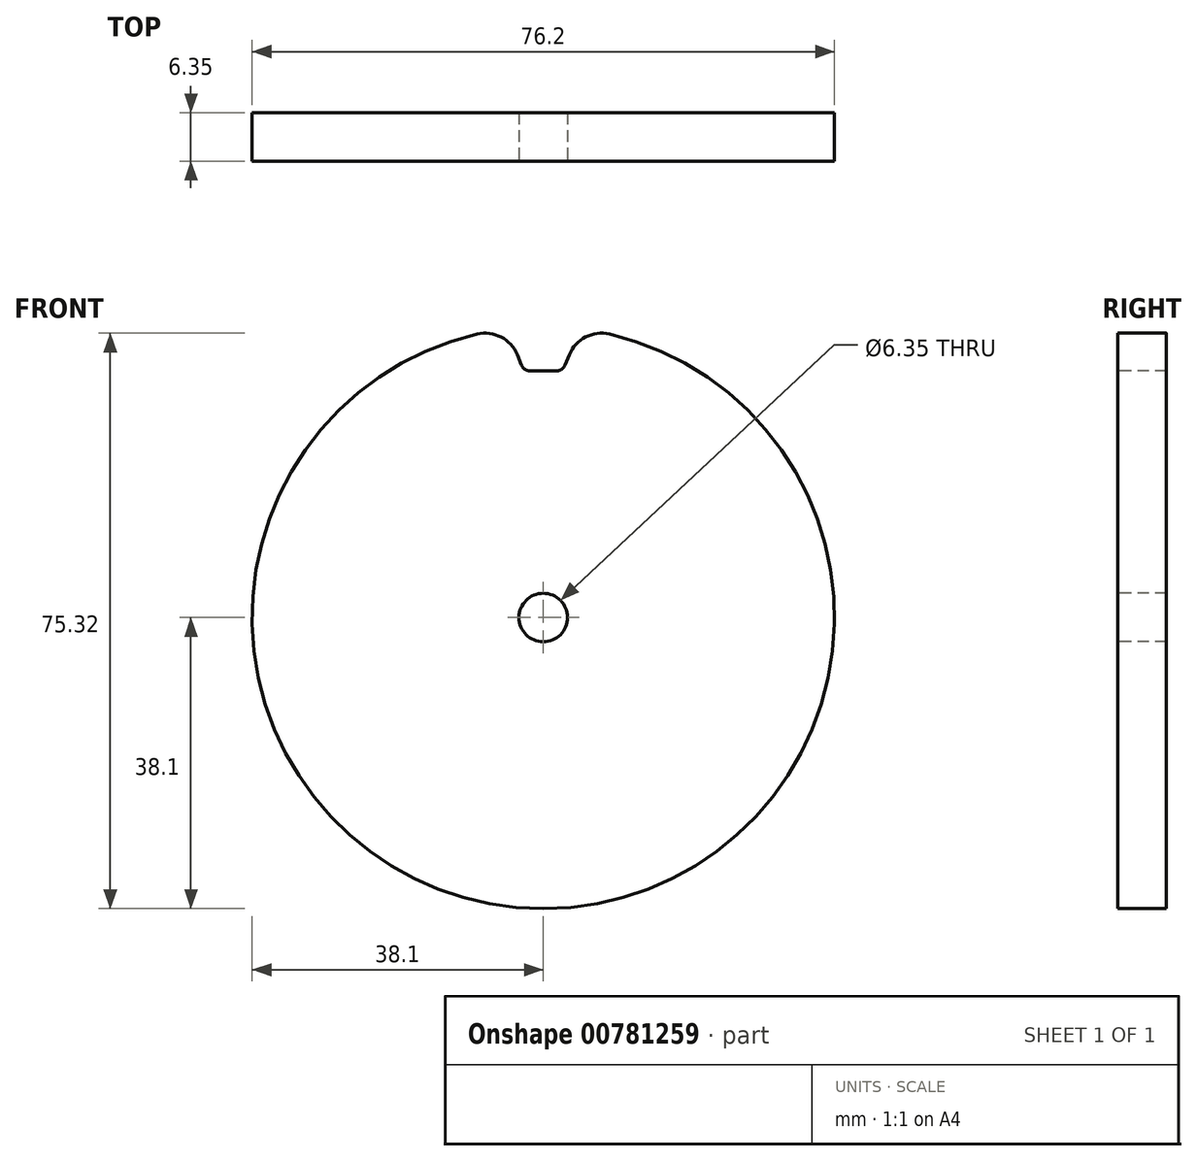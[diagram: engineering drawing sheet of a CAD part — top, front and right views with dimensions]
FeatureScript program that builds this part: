
annotation { "Feature Type Name" : "Feature", "Feature Type Description" : "" }
export const myFeature = defineFeature(function(context is Context, id is Id, definition is map)
    precondition{}
    {
        {
            var Q0;
            Q0=qCreatedBy(makeId("Right.planeOp"),FACE);
            var sketch = newSketch(context, id + "F0", { "sketchPlane" : qUnion([Q0])});
            skLineSegment(sketch, "E0", {"start": v(0, 0) * mm, "end": v(0, 76.2) * mm});
            skLineSegment(sketch, "E1", {"start": v(0, 76.2) * mm, "end": v(6.35, 76.2) * mm});
            skLineSegment(sketch, "E2", {"start": v(6.35, 76.2) * mm, "end": v(6.35, 0) * mm});
            skLineSegment(sketch, "E3", {"start": v(6.35, 0) * mm, "end": v(0, 0) * mm});
            skLineSegment(sketch, "E4", {"start": v(0, 38.1) * mm, "end": v(6.35, 38.1) * mm});
            skSolve(sketch);
        }
        {
            var Q0;
            {var subQ0=sQuery(id+"F0.wireOp",EDGE,"E1");Q0=makeQuery(id+"F0.imprint","IMPRINT",FACE,{"disambiguationData":[TD([[makeQuery(id+"F0.imprint","IMPRINT",EDGE,{"derivedFrom":subQ0}),-1.0]])]});}
            var Q1;
            Q1=sQuery(id+"F0.wireOp",EDGE,"E4");
            revolve(context, id + "F1", {"surfaceOperationType" : NewSurfaceOperationType.NEW, "entities" : qUnion([Q0]), "axis" : qUnion([Q1]), "revolveType" : RevolveType.FULL});
        }
        {
            var Q0;
            Q0=qCreatedBy(makeId("Front.planeOp"),FACE);
            var sketch = newSketch(context, id + "F2", { "sketchPlane" : qUnion([Q0])});
            skLineSegment(sketch, "E5", {"start": v(0, 0) * mm, "end": v(0, 76.2) * mm});
            skLineSegment(sketch, "E6", {"start": v(0, 70.36) * mm, "end": v(1.69, 70.36) * mm});
            skLineSegment(sketch, "E7", {"start": v(2.86, 71.16) * mm, "end": v(4.92, 76.2) * mm});
            skLineSegment(sketch, "E8.MirrorCS", {"start": v(0, 70.36) * mm, "end": v(-1.69, 70.36) * mm});
            skLineSegment(sketch, "E9.MirrorCS", {"start": v(-2.86, 71.16) * mm, "end": v(-4.92, 76.2) * mm});
            skLineSegment(sketch, "E10", {"start": v(-4.92, 76.2) * mm, "end": v(0, 76.2) * mm});
            skLineSegment(sketch, "E11", {"start": v(4.92, 76.2) * mm, "end": v(0, 76.2) * mm});
            skPoint(sketch, "E12.visualSharp", {"position": v(2.54, 70.36) * mm});
            skArc(sketch, "E12.filletArc", {"start": v(1.69, 70.36) * mm, "mid": v(2.4, 70.58) * mm, "end": v(2.86, 71.16) * mm});
            skPoint(sketch, "E13.visualSharp", {"position": v(-2.54, 70.36) * mm});
            skArc(sketch, "E13.filletArc", {"start": v(-2.86, 71.16) * mm, "mid": v(-2.4, 70.58) * mm, "end": v(-1.69, 70.36) * mm});
            skSolve(sketch);
        }
        {
            var Q0;
            {var subQ2=sQuery(id+"F2.wireOp",EDGE,"E8.MirrorCS");Q0=makeQuery(id+"F2.imprint","IMPRINT",FACE,{"disambiguationData":[TD([[makeQuery(id+"F2.imprint","IMPRINT",EDGE,{"derivedFrom":subQ2}),-1.0]])]});}
            var Q1;
            {var subQ2=sQuery(id+"F2.wireOp",EDGE,"E6");Q1=makeQuery(id+"F2.imprint","IMPRINT",FACE,{"disambiguationData":[TD([[makeQuery(id+"F2.imprint","IMPRINT",EDGE,{"derivedFrom":subQ2}),1.0]])]});}
            extrude(context, id + "F3", {"entities" : qUnion([Q0, Q1]), "operationType" : NewBodyOperationType.REMOVE, "oppositeDirection" : true, "depth" : 6.35 * mm, "offsetDistance" : 25.4 * mm});
        }
        {
            var Q0;
            {var subQ0=sQuery(id+"F2.wireOp",EDGE,"E9.MirrorCS");var subQ4=makeQuery(id+"F3.boolean.opBoolean","COPY",FACE,{"derivedFrom":makeQuery(id+"F3.opExtrude","SWEPT_FACE",FACE,{"disambiguationData":[OSD([subQ0])]})});Q0=makeQuery(id+"FfLhC88wAqj1xS8_1.13.F3.boolean.opBoolean","INTERSECT",EDGE,{"derivedFrom":[makeQuery(id+"FfLhC88wAqj1xS8_1.12.F3.boolean.opBoolean","SPLIT",FACE,{"disambiguationData":[TD([subQ4])],"derivedFrom":makeQuery(id+"FfLhC88wAqj1xS8_1.11.F3.boolean.opBoolean","SPLIT",FACE,{"disambiguationData":[TD([subQ4])],"derivedFrom":makeQuery(id+"FfLhC88wAqj1xS8_1.10.F3.boolean.opBoolean","SPLIT",FACE,{"disambiguationData":[TD([subQ4])],"derivedFrom":makeQuery(id+"FfLhC88wAqj1xS8_1.9.F3.boolean.opBoolean","SPLIT",FACE,{"disambiguationData":[TD([subQ4])],"derivedFrom":makeQuery(id+"FfLhC88wAqj1xS8_1.8.F3.boolean.opBoolean","SPLIT",FACE,{"disambiguationData":[TD([subQ4])],"derivedFrom":makeQuery(id+"FfLhC88wAqj1xS8_1.7.F3.boolean.opBoolean","SPLIT",FACE,{"disambiguationData":[TD([subQ4])],"derivedFrom":makeQuery(id+"FfLhC88wAqj1xS8_1.6.F3.boolean.opBoolean","SPLIT",FACE,{"disambiguationData":[TD([subQ4])],"derivedFrom":makeQuery(id+"FfLhC88wAqj1xS8_1.5.F3.boolean.opBoolean","SPLIT",FACE,{"disambiguationData":[TD([subQ4])],"derivedFrom":makeQuery(id+"FfLhC88wAqj1xS8_1.4.F3.boolean.opBoolean","SPLIT",FACE,{"disambiguationData":[TD([subQ4])],"derivedFrom":makeQuery(id+"FfLhC88wAqj1xS8_1.3.F3.boolean.opBoolean","SPLIT",FACE,{"disambiguationData":[TD([subQ4])],"derivedFrom":makeQuery(id+"FfLhC88wAqj1xS8_1.2.F3.boolean.opBoolean","SPLIT",FACE,{"disambiguationData":[TD([subQ4])],"derivedFrom":makeQuery(id+"FfLhC88wAqj1xS8_1.1.F3.boolean.opBoolean","SPLIT",FACE,{"disambiguationData":[TD([subQ4])],"derivedFrom":makeQuery(id+"F1.opRevolve","SWEPT_FACE",FACE,{"disambiguationData":[OSD([sQuery(id+"F0.wireOp",EDGE,"E1")])]})})})})})})})})})})})})}),makeQuery(id+"FfLhC88wAqj1xS8_1.13.F3.opExtrude","SWEPT_FACE",FACE,{"disambiguationData":[OSD([subQ0])]})]});}
            var Q1;
            {var subQ0=sQuery(id+"F2.wireOp",EDGE,"E7");var subQ3=makeQuery(id+"F3.boolean.opBoolean","COPY",FACE,{"derivedFrom":makeQuery(id+"F3.opExtrude","SWEPT_FACE",FACE,{"disambiguationData":[OSD([sQuery(id+"F2.wireOp",EDGE,"E9.MirrorCS")])]})});Q1=makeQuery(id+"FfLhC88wAqj1xS8_1.13.F3.boolean.opBoolean","INTERSECT",EDGE,{"derivedFrom":[makeQuery(id+"FfLhC88wAqj1xS8_1.12.F3.boolean.opBoolean","SPLIT",FACE,{"disambiguationData":[TD([subQ3])],"derivedFrom":makeQuery(id+"FfLhC88wAqj1xS8_1.11.F3.boolean.opBoolean","SPLIT",FACE,{"disambiguationData":[TD([subQ3])],"derivedFrom":makeQuery(id+"FfLhC88wAqj1xS8_1.10.F3.boolean.opBoolean","SPLIT",FACE,{"disambiguationData":[TD([subQ3])],"derivedFrom":makeQuery(id+"FfLhC88wAqj1xS8_1.9.F3.boolean.opBoolean","SPLIT",FACE,{"disambiguationData":[TD([subQ3])],"derivedFrom":makeQuery(id+"FfLhC88wAqj1xS8_1.8.F3.boolean.opBoolean","SPLIT",FACE,{"disambiguationData":[TD([subQ3])],"derivedFrom":makeQuery(id+"FfLhC88wAqj1xS8_1.7.F3.boolean.opBoolean","SPLIT",FACE,{"disambiguationData":[TD([subQ3])],"derivedFrom":makeQuery(id+"FfLhC88wAqj1xS8_1.6.F3.boolean.opBoolean","SPLIT",FACE,{"disambiguationData":[TD([subQ3])],"derivedFrom":makeQuery(id+"FfLhC88wAqj1xS8_1.5.F3.boolean.opBoolean","SPLIT",FACE,{"disambiguationData":[TD([subQ3])],"derivedFrom":makeQuery(id+"FfLhC88wAqj1xS8_1.4.F3.boolean.opBoolean","SPLIT",FACE,{"disambiguationData":[TD([subQ3])],"derivedFrom":makeQuery(id+"FfLhC88wAqj1xS8_1.3.F3.boolean.opBoolean","SPLIT",FACE,{"disambiguationData":[TD([subQ3])],"derivedFrom":makeQuery(id+"FfLhC88wAqj1xS8_1.2.F3.boolean.opBoolean","SPLIT",FACE,{"disambiguationData":[TD([subQ3])],"derivedFrom":makeQuery(id+"FfLhC88wAqj1xS8_1.1.F3.boolean.opBoolean","SPLIT",FACE,{"disambiguationData":[TD([subQ3])],"derivedFrom":makeQuery(id+"F1.opRevolve","SWEPT_FACE",FACE,{"disambiguationData":[OSD([sQuery(id+"F0.wireOp",EDGE,"E1")])]})})})})})})})})})})})})}),makeQuery(id+"FfLhC88wAqj1xS8_1.13.F3.opExtrude","SWEPT_FACE",FACE,{"disambiguationData":[OSD([subQ0])]})]});}
            var Q2;
            {var subQ0=sQuery(id+"F2.wireOp",EDGE,"E9.MirrorCS");var subQ4=makeQuery(id+"F3.boolean.opBoolean","COPY",FACE,{"derivedFrom":makeQuery(id+"F3.opExtrude","SWEPT_FACE",FACE,{"disambiguationData":[OSD([subQ0])]})});Q2=makeQuery(id+"FfLhC88wAqj1xS8_1.14.F3.boolean.opBoolean","INTERSECT",EDGE,{"derivedFrom":[makeQuery(id+"FfLhC88wAqj1xS8_1.13.F3.boolean.opBoolean","SPLIT",FACE,{"disambiguationData":[TD([subQ4])],"derivedFrom":makeQuery(id+"FfLhC88wAqj1xS8_1.12.F3.boolean.opBoolean","SPLIT",FACE,{"disambiguationData":[TD([subQ4])],"derivedFrom":makeQuery(id+"FfLhC88wAqj1xS8_1.11.F3.boolean.opBoolean","SPLIT",FACE,{"disambiguationData":[TD([subQ4])],"derivedFrom":makeQuery(id+"FfLhC88wAqj1xS8_1.10.F3.boolean.opBoolean","SPLIT",FACE,{"disambiguationData":[TD([subQ4])],"derivedFrom":makeQuery(id+"FfLhC88wAqj1xS8_1.9.F3.boolean.opBoolean","SPLIT",FACE,{"disambiguationData":[TD([subQ4])],"derivedFrom":makeQuery(id+"FfLhC88wAqj1xS8_1.8.F3.boolean.opBoolean","SPLIT",FACE,{"disambiguationData":[TD([subQ4])],"derivedFrom":makeQuery(id+"FfLhC88wAqj1xS8_1.7.F3.boolean.opBoolean","SPLIT",FACE,{"disambiguationData":[TD([subQ4])],"derivedFrom":makeQuery(id+"FfLhC88wAqj1xS8_1.6.F3.boolean.opBoolean","SPLIT",FACE,{"disambiguationData":[TD([subQ4])],"derivedFrom":makeQuery(id+"FfLhC88wAqj1xS8_1.5.F3.boolean.opBoolean","SPLIT",FACE,{"disambiguationData":[TD([subQ4])],"derivedFrom":makeQuery(id+"FfLhC88wAqj1xS8_1.4.F3.boolean.opBoolean","SPLIT",FACE,{"disambiguationData":[TD([subQ4])],"derivedFrom":makeQuery(id+"FfLhC88wAqj1xS8_1.3.F3.boolean.opBoolean","SPLIT",FACE,{"disambiguationData":[TD([subQ4])],"derivedFrom":makeQuery(id+"FfLhC88wAqj1xS8_1.2.F3.boolean.opBoolean","SPLIT",FACE,{"disambiguationData":[TD([subQ4])],"derivedFrom":makeQuery(id+"FfLhC88wAqj1xS8_1.1.F3.boolean.opBoolean","SPLIT",FACE,{"disambiguationData":[TD([subQ4])],"derivedFrom":makeQuery(id+"F1.opRevolve","SWEPT_FACE",FACE,{"disambiguationData":[OSD([sQuery(id+"F0.wireOp",EDGE,"E1")])]})})})})})})})})})})})})})}),makeQuery(id+"FfLhC88wAqj1xS8_1.14.F3.opExtrude","SWEPT_FACE",FACE,{"disambiguationData":[OSD([subQ0])]})]});}
            var Q3;
            {var subQ0=sQuery(id+"F2.wireOp",EDGE,"E7");var subQ3=makeQuery(id+"F3.boolean.opBoolean","COPY",FACE,{"derivedFrom":makeQuery(id+"F3.opExtrude","SWEPT_FACE",FACE,{"disambiguationData":[OSD([sQuery(id+"F2.wireOp",EDGE,"E9.MirrorCS")])]})});Q3=makeQuery(id+"FfLhC88wAqj1xS8_1.14.F3.boolean.opBoolean","INTERSECT",EDGE,{"derivedFrom":[makeQuery(id+"FfLhC88wAqj1xS8_1.13.F3.boolean.opBoolean","SPLIT",FACE,{"disambiguationData":[TD([subQ3])],"derivedFrom":makeQuery(id+"FfLhC88wAqj1xS8_1.12.F3.boolean.opBoolean","SPLIT",FACE,{"disambiguationData":[TD([subQ3])],"derivedFrom":makeQuery(id+"FfLhC88wAqj1xS8_1.11.F3.boolean.opBoolean","SPLIT",FACE,{"disambiguationData":[TD([subQ3])],"derivedFrom":makeQuery(id+"FfLhC88wAqj1xS8_1.10.F3.boolean.opBoolean","SPLIT",FACE,{"disambiguationData":[TD([subQ3])],"derivedFrom":makeQuery(id+"FfLhC88wAqj1xS8_1.9.F3.boolean.opBoolean","SPLIT",FACE,{"disambiguationData":[TD([subQ3])],"derivedFrom":makeQuery(id+"FfLhC88wAqj1xS8_1.8.F3.boolean.opBoolean","SPLIT",FACE,{"disambiguationData":[TD([subQ3])],"derivedFrom":makeQuery(id+"FfLhC88wAqj1xS8_1.7.F3.boolean.opBoolean","SPLIT",FACE,{"disambiguationData":[TD([subQ3])],"derivedFrom":makeQuery(id+"FfLhC88wAqj1xS8_1.6.F3.boolean.opBoolean","SPLIT",FACE,{"disambiguationData":[TD([subQ3])],"derivedFrom":makeQuery(id+"FfLhC88wAqj1xS8_1.5.F3.boolean.opBoolean","SPLIT",FACE,{"disambiguationData":[TD([subQ3])],"derivedFrom":makeQuery(id+"FfLhC88wAqj1xS8_1.4.F3.boolean.opBoolean","SPLIT",FACE,{"disambiguationData":[TD([subQ3])],"derivedFrom":makeQuery(id+"FfLhC88wAqj1xS8_1.3.F3.boolean.opBoolean","SPLIT",FACE,{"disambiguationData":[TD([subQ3])],"derivedFrom":makeQuery(id+"FfLhC88wAqj1xS8_1.2.F3.boolean.opBoolean","SPLIT",FACE,{"disambiguationData":[TD([subQ3])],"derivedFrom":makeQuery(id+"FfLhC88wAqj1xS8_1.1.F3.boolean.opBoolean","SPLIT",FACE,{"disambiguationData":[TD([subQ3])],"derivedFrom":makeQuery(id+"F1.opRevolve","SWEPT_FACE",FACE,{"disambiguationData":[OSD([sQuery(id+"F0.wireOp",EDGE,"E1")])]})})})})})})})})})})})})})}),makeQuery(id+"FfLhC88wAqj1xS8_1.14.F3.opExtrude","SWEPT_FACE",FACE,{"disambiguationData":[OSD([subQ0])]})]});}
            var Q4;
            {var subQ0=sQuery(id+"F2.wireOp",EDGE,"E9.MirrorCS");var subQ3=makeQuery(id+"F3.boolean.opBoolean","COPY",FACE,{"derivedFrom":makeQuery(id+"F3.opExtrude","SWEPT_FACE",FACE,{"disambiguationData":[OSD([subQ0])]})});Q4=makeQuery(id+"FfLhC88wAqj1xS8_1.15.F3.boolean.opBoolean","INTERSECT",EDGE,{"derivedFrom":[makeQuery(id+"FfLhC88wAqj1xS8_1.14.F3.boolean.opBoolean","SPLIT",FACE,{"disambiguationData":[TD([subQ3])],"derivedFrom":makeQuery(id+"FfLhC88wAqj1xS8_1.13.F3.boolean.opBoolean","SPLIT",FACE,{"disambiguationData":[TD([subQ3])],"derivedFrom":makeQuery(id+"FfLhC88wAqj1xS8_1.12.F3.boolean.opBoolean","SPLIT",FACE,{"disambiguationData":[TD([subQ3])],"derivedFrom":makeQuery(id+"FfLhC88wAqj1xS8_1.11.F3.boolean.opBoolean","SPLIT",FACE,{"disambiguationData":[TD([subQ3])],"derivedFrom":makeQuery(id+"FfLhC88wAqj1xS8_1.10.F3.boolean.opBoolean","SPLIT",FACE,{"disambiguationData":[TD([subQ3])],"derivedFrom":makeQuery(id+"FfLhC88wAqj1xS8_1.9.F3.boolean.opBoolean","SPLIT",FACE,{"disambiguationData":[TD([subQ3])],"derivedFrom":makeQuery(id+"FfLhC88wAqj1xS8_1.8.F3.boolean.opBoolean","SPLIT",FACE,{"disambiguationData":[TD([subQ3])],"derivedFrom":makeQuery(id+"FfLhC88wAqj1xS8_1.7.F3.boolean.opBoolean","SPLIT",FACE,{"disambiguationData":[TD([subQ3])],"derivedFrom":makeQuery(id+"FfLhC88wAqj1xS8_1.6.F3.boolean.opBoolean","SPLIT",FACE,{"disambiguationData":[TD([subQ3])],"derivedFrom":makeQuery(id+"FfLhC88wAqj1xS8_1.5.F3.boolean.opBoolean","SPLIT",FACE,{"disambiguationData":[TD([subQ3])],"derivedFrom":makeQuery(id+"FfLhC88wAqj1xS8_1.4.F3.boolean.opBoolean","SPLIT",FACE,{"disambiguationData":[TD([subQ3])],"derivedFrom":makeQuery(id+"FfLhC88wAqj1xS8_1.3.F3.boolean.opBoolean","SPLIT",FACE,{"disambiguationData":[TD([subQ3])],"derivedFrom":makeQuery(id+"FfLhC88wAqj1xS8_1.2.F3.boolean.opBoolean","SPLIT",FACE,{"disambiguationData":[TD([subQ3])],"derivedFrom":makeQuery(id+"FfLhC88wAqj1xS8_1.1.F3.boolean.opBoolean","SPLIT",FACE,{"disambiguationData":[TD([subQ3])],"derivedFrom":makeQuery(id+"F1.opRevolve","SWEPT_FACE",FACE,{"disambiguationData":[OSD([sQuery(id+"F0.wireOp",EDGE,"E1")])]})})})})})})})})})})})})})})}),makeQuery(id+"FfLhC88wAqj1xS8_1.15.F3.opExtrude","SWEPT_FACE",FACE,{"disambiguationData":[OSD([subQ0])]})]});}
            var Q5;
            {var subQ0=sQuery(id+"F2.wireOp",EDGE,"E7");var subQ3=makeQuery(id+"F3.boolean.opBoolean","COPY",FACE,{"derivedFrom":makeQuery(id+"F3.opExtrude","SWEPT_FACE",FACE,{"disambiguationData":[OSD([sQuery(id+"F2.wireOp",EDGE,"E9.MirrorCS")])]})});Q5=makeQuery(id+"FfLhC88wAqj1xS8_1.15.F3.boolean.opBoolean","INTERSECT",EDGE,{"derivedFrom":[makeQuery(id+"FfLhC88wAqj1xS8_1.14.F3.boolean.opBoolean","SPLIT",FACE,{"disambiguationData":[TD([subQ3])],"derivedFrom":makeQuery(id+"FfLhC88wAqj1xS8_1.13.F3.boolean.opBoolean","SPLIT",FACE,{"disambiguationData":[TD([subQ3])],"derivedFrom":makeQuery(id+"FfLhC88wAqj1xS8_1.12.F3.boolean.opBoolean","SPLIT",FACE,{"disambiguationData":[TD([subQ3])],"derivedFrom":makeQuery(id+"FfLhC88wAqj1xS8_1.11.F3.boolean.opBoolean","SPLIT",FACE,{"disambiguationData":[TD([subQ3])],"derivedFrom":makeQuery(id+"FfLhC88wAqj1xS8_1.10.F3.boolean.opBoolean","SPLIT",FACE,{"disambiguationData":[TD([subQ3])],"derivedFrom":makeQuery(id+"FfLhC88wAqj1xS8_1.9.F3.boolean.opBoolean","SPLIT",FACE,{"disambiguationData":[TD([subQ3])],"derivedFrom":makeQuery(id+"FfLhC88wAqj1xS8_1.8.F3.boolean.opBoolean","SPLIT",FACE,{"disambiguationData":[TD([subQ3])],"derivedFrom":makeQuery(id+"FfLhC88wAqj1xS8_1.7.F3.boolean.opBoolean","SPLIT",FACE,{"disambiguationData":[TD([subQ3])],"derivedFrom":makeQuery(id+"FfLhC88wAqj1xS8_1.6.F3.boolean.opBoolean","SPLIT",FACE,{"disambiguationData":[TD([subQ3])],"derivedFrom":makeQuery(id+"FfLhC88wAqj1xS8_1.5.F3.boolean.opBoolean","SPLIT",FACE,{"disambiguationData":[TD([subQ3])],"derivedFrom":makeQuery(id+"FfLhC88wAqj1xS8_1.4.F3.boolean.opBoolean","SPLIT",FACE,{"disambiguationData":[TD([subQ3])],"derivedFrom":makeQuery(id+"FfLhC88wAqj1xS8_1.3.F3.boolean.opBoolean","SPLIT",FACE,{"disambiguationData":[TD([subQ3])],"derivedFrom":makeQuery(id+"FfLhC88wAqj1xS8_1.2.F3.boolean.opBoolean","SPLIT",FACE,{"disambiguationData":[TD([subQ3])],"derivedFrom":makeQuery(id+"FfLhC88wAqj1xS8_1.1.F3.boolean.opBoolean","SPLIT",FACE,{"disambiguationData":[TD([subQ3])],"derivedFrom":makeQuery(id+"F1.opRevolve","SWEPT_FACE",FACE,{"disambiguationData":[OSD([sQuery(id+"F0.wireOp",EDGE,"E1")])]})})})})})})})})})})})})})})}),makeQuery(id+"FfLhC88wAqj1xS8_1.15.F3.opExtrude","SWEPT_FACE",FACE,{"disambiguationData":[OSD([subQ0])]})]});}
            var Q6;
            Q6=makeQuery(id+"F3.boolean.opBoolean","INTERSECT",EDGE,{"derivedFrom":[makeQuery(id+"F1.opRevolve","SWEPT_FACE",FACE,{"disambiguationData":[OSD([sQuery(id+"F0.wireOp",EDGE,"E1")])]}),makeQuery(id+"F3.opExtrude","SWEPT_FACE",FACE,{"disambiguationData":[OSD([sQuery(id+"F2.wireOp",EDGE,"E9.MirrorCS")])]})]});
            var Q7;
            Q7=makeQuery(id+"F3.boolean.opBoolean","INTERSECT",EDGE,{"derivedFrom":[makeQuery(id+"F1.opRevolve","SWEPT_FACE",FACE,{"disambiguationData":[OSD([sQuery(id+"F0.wireOp",EDGE,"E1")])]}),makeQuery(id+"F3.opExtrude","SWEPT_FACE",FACE,{"disambiguationData":[OSD([sQuery(id+"F2.wireOp",EDGE,"E7")])]})]});
            var Q8;
            {var subQ0=sQuery(id+"F2.wireOp",EDGE,"E7");var subQ3=makeQuery(id+"F3.boolean.opBoolean","COPY",FACE,{"derivedFrom":makeQuery(id+"F3.opExtrude","SWEPT_FACE",FACE,{"disambiguationData":[OSD([sQuery(id+"F2.wireOp",EDGE,"E9.MirrorCS")])]})});Q8=makeQuery(id+"FfLhC88wAqj1xS8_1.12.F3.boolean.opBoolean","INTERSECT",EDGE,{"derivedFrom":[makeQuery(id+"FfLhC88wAqj1xS8_1.11.F3.boolean.opBoolean","SPLIT",FACE,{"disambiguationData":[TD([subQ3])],"derivedFrom":makeQuery(id+"FfLhC88wAqj1xS8_1.10.F3.boolean.opBoolean","SPLIT",FACE,{"disambiguationData":[TD([subQ3])],"derivedFrom":makeQuery(id+"FfLhC88wAqj1xS8_1.9.F3.boolean.opBoolean","SPLIT",FACE,{"disambiguationData":[TD([subQ3])],"derivedFrom":makeQuery(id+"FfLhC88wAqj1xS8_1.8.F3.boolean.opBoolean","SPLIT",FACE,{"disambiguationData":[TD([subQ3])],"derivedFrom":makeQuery(id+"FfLhC88wAqj1xS8_1.7.F3.boolean.opBoolean","SPLIT",FACE,{"disambiguationData":[TD([subQ3])],"derivedFrom":makeQuery(id+"FfLhC88wAqj1xS8_1.6.F3.boolean.opBoolean","SPLIT",FACE,{"disambiguationData":[TD([subQ3])],"derivedFrom":makeQuery(id+"FfLhC88wAqj1xS8_1.5.F3.boolean.opBoolean","SPLIT",FACE,{"disambiguationData":[TD([subQ3])],"derivedFrom":makeQuery(id+"FfLhC88wAqj1xS8_1.4.F3.boolean.opBoolean","SPLIT",FACE,{"disambiguationData":[TD([subQ3])],"derivedFrom":makeQuery(id+"FfLhC88wAqj1xS8_1.3.F3.boolean.opBoolean","SPLIT",FACE,{"disambiguationData":[TD([subQ3])],"derivedFrom":makeQuery(id+"FfLhC88wAqj1xS8_1.2.F3.boolean.opBoolean","SPLIT",FACE,{"disambiguationData":[TD([subQ3])],"derivedFrom":makeQuery(id+"FfLhC88wAqj1xS8_1.1.F3.boolean.opBoolean","SPLIT",FACE,{"disambiguationData":[TD([subQ3])],"derivedFrom":makeQuery(id+"F1.opRevolve","SWEPT_FACE",FACE,{"disambiguationData":[OSD([sQuery(id+"F0.wireOp",EDGE,"E1")])]})})})})})})})})})})})}),makeQuery(id+"FfLhC88wAqj1xS8_1.12.F3.opExtrude","SWEPT_FACE",FACE,{"disambiguationData":[OSD([subQ0])]})]});}
            var Q9;
            {var subQ0=sQuery(id+"F2.wireOp",EDGE,"E9.MirrorCS");var subQ3=makeQuery(id+"F3.boolean.opBoolean","COPY",FACE,{"derivedFrom":makeQuery(id+"F3.opExtrude","SWEPT_FACE",FACE,{"disambiguationData":[OSD([subQ0])]})});Q9=makeQuery(id+"FfLhC88wAqj1xS8_1.12.F3.boolean.opBoolean","INTERSECT",EDGE,{"derivedFrom":[makeQuery(id+"FfLhC88wAqj1xS8_1.11.F3.boolean.opBoolean","SPLIT",FACE,{"disambiguationData":[TD([subQ3])],"derivedFrom":makeQuery(id+"FfLhC88wAqj1xS8_1.10.F3.boolean.opBoolean","SPLIT",FACE,{"disambiguationData":[TD([subQ3])],"derivedFrom":makeQuery(id+"FfLhC88wAqj1xS8_1.9.F3.boolean.opBoolean","SPLIT",FACE,{"disambiguationData":[TD([subQ3])],"derivedFrom":makeQuery(id+"FfLhC88wAqj1xS8_1.8.F3.boolean.opBoolean","SPLIT",FACE,{"disambiguationData":[TD([subQ3])],"derivedFrom":makeQuery(id+"FfLhC88wAqj1xS8_1.7.F3.boolean.opBoolean","SPLIT",FACE,{"disambiguationData":[TD([subQ3])],"derivedFrom":makeQuery(id+"FfLhC88wAqj1xS8_1.6.F3.boolean.opBoolean","SPLIT",FACE,{"disambiguationData":[TD([subQ3])],"derivedFrom":makeQuery(id+"FfLhC88wAqj1xS8_1.5.F3.boolean.opBoolean","SPLIT",FACE,{"disambiguationData":[TD([subQ3])],"derivedFrom":makeQuery(id+"FfLhC88wAqj1xS8_1.4.F3.boolean.opBoolean","SPLIT",FACE,{"disambiguationData":[TD([subQ3])],"derivedFrom":makeQuery(id+"FfLhC88wAqj1xS8_1.3.F3.boolean.opBoolean","SPLIT",FACE,{"disambiguationData":[TD([subQ3])],"derivedFrom":makeQuery(id+"FfLhC88wAqj1xS8_1.2.F3.boolean.opBoolean","SPLIT",FACE,{"disambiguationData":[TD([subQ3])],"derivedFrom":makeQuery(id+"FfLhC88wAqj1xS8_1.1.F3.boolean.opBoolean","SPLIT",FACE,{"disambiguationData":[TD([subQ3])],"derivedFrom":makeQuery(id+"F1.opRevolve","SWEPT_FACE",FACE,{"disambiguationData":[OSD([sQuery(id+"F0.wireOp",EDGE,"E1")])]})})})})})})})})})})})}),makeQuery(id+"FfLhC88wAqj1xS8_1.12.F3.opExtrude","SWEPT_FACE",FACE,{"disambiguationData":[OSD([subQ0])]})]});}
            var Q10;
            {var subQ0=sQuery(id+"F2.wireOp",EDGE,"E7");var subQ3=makeQuery(id+"F3.boolean.opBoolean","COPY",FACE,{"derivedFrom":makeQuery(id+"F3.opExtrude","SWEPT_FACE",FACE,{"disambiguationData":[OSD([sQuery(id+"F2.wireOp",EDGE,"E9.MirrorCS")])]})});Q10=makeQuery(id+"FfLhC88wAqj1xS8_1.11.F3.boolean.opBoolean","INTERSECT",EDGE,{"derivedFrom":[makeQuery(id+"FfLhC88wAqj1xS8_1.10.F3.boolean.opBoolean","SPLIT",FACE,{"disambiguationData":[TD([subQ3])],"derivedFrom":makeQuery(id+"FfLhC88wAqj1xS8_1.9.F3.boolean.opBoolean","SPLIT",FACE,{"disambiguationData":[TD([subQ3])],"derivedFrom":makeQuery(id+"FfLhC88wAqj1xS8_1.8.F3.boolean.opBoolean","SPLIT",FACE,{"disambiguationData":[TD([subQ3])],"derivedFrom":makeQuery(id+"FfLhC88wAqj1xS8_1.7.F3.boolean.opBoolean","SPLIT",FACE,{"disambiguationData":[TD([subQ3])],"derivedFrom":makeQuery(id+"FfLhC88wAqj1xS8_1.6.F3.boolean.opBoolean","SPLIT",FACE,{"disambiguationData":[TD([subQ3])],"derivedFrom":makeQuery(id+"FfLhC88wAqj1xS8_1.5.F3.boolean.opBoolean","SPLIT",FACE,{"disambiguationData":[TD([subQ3])],"derivedFrom":makeQuery(id+"FfLhC88wAqj1xS8_1.4.F3.boolean.opBoolean","SPLIT",FACE,{"disambiguationData":[TD([subQ3])],"derivedFrom":makeQuery(id+"FfLhC88wAqj1xS8_1.3.F3.boolean.opBoolean","SPLIT",FACE,{"disambiguationData":[TD([subQ3])],"derivedFrom":makeQuery(id+"FfLhC88wAqj1xS8_1.2.F3.boolean.opBoolean","SPLIT",FACE,{"disambiguationData":[TD([subQ3])],"derivedFrom":makeQuery(id+"FfLhC88wAqj1xS8_1.1.F3.boolean.opBoolean","SPLIT",FACE,{"disambiguationData":[TD([subQ3])],"derivedFrom":makeQuery(id+"F1.opRevolve","SWEPT_FACE",FACE,{"disambiguationData":[OSD([sQuery(id+"F0.wireOp",EDGE,"E1")])]})})})})})})})})})})}),makeQuery(id+"FfLhC88wAqj1xS8_1.11.F3.opExtrude","SWEPT_FACE",FACE,{"disambiguationData":[OSD([subQ0])]})]});}
            var Q11;
            {var subQ0=sQuery(id+"F2.wireOp",EDGE,"E9.MirrorCS");var subQ3=makeQuery(id+"F3.boolean.opBoolean","COPY",FACE,{"derivedFrom":makeQuery(id+"F3.opExtrude","SWEPT_FACE",FACE,{"disambiguationData":[OSD([subQ0])]})});Q11=makeQuery(id+"FfLhC88wAqj1xS8_1.11.F3.boolean.opBoolean","INTERSECT",EDGE,{"derivedFrom":[makeQuery(id+"FfLhC88wAqj1xS8_1.10.F3.boolean.opBoolean","SPLIT",FACE,{"disambiguationData":[TD([subQ3])],"derivedFrom":makeQuery(id+"FfLhC88wAqj1xS8_1.9.F3.boolean.opBoolean","SPLIT",FACE,{"disambiguationData":[TD([subQ3])],"derivedFrom":makeQuery(id+"FfLhC88wAqj1xS8_1.8.F3.boolean.opBoolean","SPLIT",FACE,{"disambiguationData":[TD([subQ3])],"derivedFrom":makeQuery(id+"FfLhC88wAqj1xS8_1.7.F3.boolean.opBoolean","SPLIT",FACE,{"disambiguationData":[TD([subQ3])],"derivedFrom":makeQuery(id+"FfLhC88wAqj1xS8_1.6.F3.boolean.opBoolean","SPLIT",FACE,{"disambiguationData":[TD([subQ3])],"derivedFrom":makeQuery(id+"FfLhC88wAqj1xS8_1.5.F3.boolean.opBoolean","SPLIT",FACE,{"disambiguationData":[TD([subQ3])],"derivedFrom":makeQuery(id+"FfLhC88wAqj1xS8_1.4.F3.boolean.opBoolean","SPLIT",FACE,{"disambiguationData":[TD([subQ3])],"derivedFrom":makeQuery(id+"FfLhC88wAqj1xS8_1.3.F3.boolean.opBoolean","SPLIT",FACE,{"disambiguationData":[TD([subQ3])],"derivedFrom":makeQuery(id+"FfLhC88wAqj1xS8_1.2.F3.boolean.opBoolean","SPLIT",FACE,{"disambiguationData":[TD([subQ3])],"derivedFrom":makeQuery(id+"FfLhC88wAqj1xS8_1.1.F3.boolean.opBoolean","SPLIT",FACE,{"disambiguationData":[TD([subQ3])],"derivedFrom":makeQuery(id+"F1.opRevolve","SWEPT_FACE",FACE,{"disambiguationData":[OSD([sQuery(id+"F0.wireOp",EDGE,"E1")])]})})})})})})})})})})}),makeQuery(id+"FfLhC88wAqj1xS8_1.11.F3.opExtrude","SWEPT_FACE",FACE,{"disambiguationData":[OSD([subQ0])]})]});}
            var Q12;
            {var subQ0=sQuery(id+"F2.wireOp",EDGE,"E7");var subQ3=makeQuery(id+"F3.boolean.opBoolean","COPY",FACE,{"derivedFrom":makeQuery(id+"F3.opExtrude","SWEPT_FACE",FACE,{"disambiguationData":[OSD([sQuery(id+"F2.wireOp",EDGE,"E9.MirrorCS")])]})});Q12=makeQuery(id+"FfLhC88wAqj1xS8_1.10.F3.boolean.opBoolean","INTERSECT",EDGE,{"derivedFrom":[makeQuery(id+"FfLhC88wAqj1xS8_1.9.F3.boolean.opBoolean","SPLIT",FACE,{"disambiguationData":[TD([subQ3])],"derivedFrom":makeQuery(id+"FfLhC88wAqj1xS8_1.8.F3.boolean.opBoolean","SPLIT",FACE,{"disambiguationData":[TD([subQ3])],"derivedFrom":makeQuery(id+"FfLhC88wAqj1xS8_1.7.F3.boolean.opBoolean","SPLIT",FACE,{"disambiguationData":[TD([subQ3])],"derivedFrom":makeQuery(id+"FfLhC88wAqj1xS8_1.6.F3.boolean.opBoolean","SPLIT",FACE,{"disambiguationData":[TD([subQ3])],"derivedFrom":makeQuery(id+"FfLhC88wAqj1xS8_1.5.F3.boolean.opBoolean","SPLIT",FACE,{"disambiguationData":[TD([subQ3])],"derivedFrom":makeQuery(id+"FfLhC88wAqj1xS8_1.4.F3.boolean.opBoolean","SPLIT",FACE,{"disambiguationData":[TD([subQ3])],"derivedFrom":makeQuery(id+"FfLhC88wAqj1xS8_1.3.F3.boolean.opBoolean","SPLIT",FACE,{"disambiguationData":[TD([subQ3])],"derivedFrom":makeQuery(id+"FfLhC88wAqj1xS8_1.2.F3.boolean.opBoolean","SPLIT",FACE,{"disambiguationData":[TD([subQ3])],"derivedFrom":makeQuery(id+"FfLhC88wAqj1xS8_1.1.F3.boolean.opBoolean","SPLIT",FACE,{"disambiguationData":[TD([subQ3])],"derivedFrom":makeQuery(id+"F1.opRevolve","SWEPT_FACE",FACE,{"disambiguationData":[OSD([sQuery(id+"F0.wireOp",EDGE,"E1")])]})})})})})})})})})}),makeQuery(id+"FfLhC88wAqj1xS8_1.10.F3.opExtrude","SWEPT_FACE",FACE,{"disambiguationData":[OSD([subQ0])]})]});}
            var Q13;
            {var subQ0=sQuery(id+"F2.wireOp",EDGE,"E9.MirrorCS");var subQ3=makeQuery(id+"F3.boolean.opBoolean","COPY",FACE,{"derivedFrom":makeQuery(id+"F3.opExtrude","SWEPT_FACE",FACE,{"disambiguationData":[OSD([subQ0])]})});Q13=makeQuery(id+"FfLhC88wAqj1xS8_1.10.F3.boolean.opBoolean","INTERSECT",EDGE,{"derivedFrom":[makeQuery(id+"FfLhC88wAqj1xS8_1.9.F3.boolean.opBoolean","SPLIT",FACE,{"disambiguationData":[TD([subQ3])],"derivedFrom":makeQuery(id+"FfLhC88wAqj1xS8_1.8.F3.boolean.opBoolean","SPLIT",FACE,{"disambiguationData":[TD([subQ3])],"derivedFrom":makeQuery(id+"FfLhC88wAqj1xS8_1.7.F3.boolean.opBoolean","SPLIT",FACE,{"disambiguationData":[TD([subQ3])],"derivedFrom":makeQuery(id+"FfLhC88wAqj1xS8_1.6.F3.boolean.opBoolean","SPLIT",FACE,{"disambiguationData":[TD([subQ3])],"derivedFrom":makeQuery(id+"FfLhC88wAqj1xS8_1.5.F3.boolean.opBoolean","SPLIT",FACE,{"disambiguationData":[TD([subQ3])],"derivedFrom":makeQuery(id+"FfLhC88wAqj1xS8_1.4.F3.boolean.opBoolean","SPLIT",FACE,{"disambiguationData":[TD([subQ3])],"derivedFrom":makeQuery(id+"FfLhC88wAqj1xS8_1.3.F3.boolean.opBoolean","SPLIT",FACE,{"disambiguationData":[TD([subQ3])],"derivedFrom":makeQuery(id+"FfLhC88wAqj1xS8_1.2.F3.boolean.opBoolean","SPLIT",FACE,{"disambiguationData":[TD([subQ3])],"derivedFrom":makeQuery(id+"FfLhC88wAqj1xS8_1.1.F3.boolean.opBoolean","SPLIT",FACE,{"disambiguationData":[TD([subQ3])],"derivedFrom":makeQuery(id+"F1.opRevolve","SWEPT_FACE",FACE,{"disambiguationData":[OSD([sQuery(id+"F0.wireOp",EDGE,"E1")])]})})})})})})})})})}),makeQuery(id+"FfLhC88wAqj1xS8_1.10.F3.opExtrude","SWEPT_FACE",FACE,{"disambiguationData":[OSD([subQ0])]})]});}
            var Q14;
            {var subQ0=sQuery(id+"F2.wireOp",EDGE,"E7");var subQ3=makeQuery(id+"F3.boolean.opBoolean","COPY",FACE,{"derivedFrom":makeQuery(id+"F3.opExtrude","SWEPT_FACE",FACE,{"disambiguationData":[OSD([sQuery(id+"F2.wireOp",EDGE,"E9.MirrorCS")])]})});Q14=makeQuery(id+"FfLhC88wAqj1xS8_1.9.F3.boolean.opBoolean","INTERSECT",EDGE,{"derivedFrom":[makeQuery(id+"FfLhC88wAqj1xS8_1.8.F3.boolean.opBoolean","SPLIT",FACE,{"disambiguationData":[TD([subQ3])],"derivedFrom":makeQuery(id+"FfLhC88wAqj1xS8_1.7.F3.boolean.opBoolean","SPLIT",FACE,{"disambiguationData":[TD([subQ3])],"derivedFrom":makeQuery(id+"FfLhC88wAqj1xS8_1.6.F3.boolean.opBoolean","SPLIT",FACE,{"disambiguationData":[TD([subQ3])],"derivedFrom":makeQuery(id+"FfLhC88wAqj1xS8_1.5.F3.boolean.opBoolean","SPLIT",FACE,{"disambiguationData":[TD([subQ3])],"derivedFrom":makeQuery(id+"FfLhC88wAqj1xS8_1.4.F3.boolean.opBoolean","SPLIT",FACE,{"disambiguationData":[TD([subQ3])],"derivedFrom":makeQuery(id+"FfLhC88wAqj1xS8_1.3.F3.boolean.opBoolean","SPLIT",FACE,{"disambiguationData":[TD([subQ3])],"derivedFrom":makeQuery(id+"FfLhC88wAqj1xS8_1.2.F3.boolean.opBoolean","SPLIT",FACE,{"disambiguationData":[TD([subQ3])],"derivedFrom":makeQuery(id+"FfLhC88wAqj1xS8_1.1.F3.boolean.opBoolean","SPLIT",FACE,{"disambiguationData":[TD([subQ3])],"derivedFrom":makeQuery(id+"F1.opRevolve","SWEPT_FACE",FACE,{"disambiguationData":[OSD([sQuery(id+"F0.wireOp",EDGE,"E1")])]})})})})})})})})}),makeQuery(id+"FfLhC88wAqj1xS8_1.9.F3.opExtrude","SWEPT_FACE",FACE,{"disambiguationData":[OSD([subQ0])]})]});}
            var Q15;
            {var subQ0=sQuery(id+"F2.wireOp",EDGE,"E9.MirrorCS");var subQ4=makeQuery(id+"F3.boolean.opBoolean","COPY",FACE,{"derivedFrom":makeQuery(id+"F3.opExtrude","SWEPT_FACE",FACE,{"disambiguationData":[OSD([subQ0])]})});Q15=makeQuery(id+"FfLhC88wAqj1xS8_1.9.F3.boolean.opBoolean","INTERSECT",EDGE,{"derivedFrom":[makeQuery(id+"FfLhC88wAqj1xS8_1.8.F3.boolean.opBoolean","SPLIT",FACE,{"disambiguationData":[TD([subQ4])],"derivedFrom":makeQuery(id+"FfLhC88wAqj1xS8_1.7.F3.boolean.opBoolean","SPLIT",FACE,{"disambiguationData":[TD([subQ4])],"derivedFrom":makeQuery(id+"FfLhC88wAqj1xS8_1.6.F3.boolean.opBoolean","SPLIT",FACE,{"disambiguationData":[TD([subQ4])],"derivedFrom":makeQuery(id+"FfLhC88wAqj1xS8_1.5.F3.boolean.opBoolean","SPLIT",FACE,{"disambiguationData":[TD([subQ4])],"derivedFrom":makeQuery(id+"FfLhC88wAqj1xS8_1.4.F3.boolean.opBoolean","SPLIT",FACE,{"disambiguationData":[TD([subQ4])],"derivedFrom":makeQuery(id+"FfLhC88wAqj1xS8_1.3.F3.boolean.opBoolean","SPLIT",FACE,{"disambiguationData":[TD([subQ4])],"derivedFrom":makeQuery(id+"FfLhC88wAqj1xS8_1.2.F3.boolean.opBoolean","SPLIT",FACE,{"disambiguationData":[TD([subQ4])],"derivedFrom":makeQuery(id+"FfLhC88wAqj1xS8_1.1.F3.boolean.opBoolean","SPLIT",FACE,{"disambiguationData":[TD([subQ4])],"derivedFrom":makeQuery(id+"F1.opRevolve","SWEPT_FACE",FACE,{"disambiguationData":[OSD([sQuery(id+"F0.wireOp",EDGE,"E1")])]})})})})})})})})}),makeQuery(id+"FfLhC88wAqj1xS8_1.9.F3.opExtrude","SWEPT_FACE",FACE,{"disambiguationData":[OSD([subQ0])]})]});}
            var Q16;
            {var subQ0=sQuery(id+"F2.wireOp",EDGE,"E7");var subQ3=makeQuery(id+"F3.boolean.opBoolean","COPY",FACE,{"derivedFrom":makeQuery(id+"F3.opExtrude","SWEPT_FACE",FACE,{"disambiguationData":[OSD([sQuery(id+"F2.wireOp",EDGE,"E9.MirrorCS")])]})});Q16=makeQuery(id+"FfLhC88wAqj1xS8_1.8.F3.boolean.opBoolean","INTERSECT",EDGE,{"derivedFrom":[makeQuery(id+"FfLhC88wAqj1xS8_1.7.F3.boolean.opBoolean","SPLIT",FACE,{"disambiguationData":[TD([subQ3])],"derivedFrom":makeQuery(id+"FfLhC88wAqj1xS8_1.6.F3.boolean.opBoolean","SPLIT",FACE,{"disambiguationData":[TD([subQ3])],"derivedFrom":makeQuery(id+"FfLhC88wAqj1xS8_1.5.F3.boolean.opBoolean","SPLIT",FACE,{"disambiguationData":[TD([subQ3])],"derivedFrom":makeQuery(id+"FfLhC88wAqj1xS8_1.4.F3.boolean.opBoolean","SPLIT",FACE,{"disambiguationData":[TD([subQ3])],"derivedFrom":makeQuery(id+"FfLhC88wAqj1xS8_1.3.F3.boolean.opBoolean","SPLIT",FACE,{"disambiguationData":[TD([subQ3])],"derivedFrom":makeQuery(id+"FfLhC88wAqj1xS8_1.2.F3.boolean.opBoolean","SPLIT",FACE,{"disambiguationData":[TD([subQ3])],"derivedFrom":makeQuery(id+"FfLhC88wAqj1xS8_1.1.F3.boolean.opBoolean","SPLIT",FACE,{"disambiguationData":[TD([subQ3])],"derivedFrom":makeQuery(id+"F1.opRevolve","SWEPT_FACE",FACE,{"disambiguationData":[OSD([sQuery(id+"F0.wireOp",EDGE,"E1")])]})})})})})})})}),makeQuery(id+"FfLhC88wAqj1xS8_1.8.F3.opExtrude","SWEPT_FACE",FACE,{"disambiguationData":[OSD([subQ0])]})]});}
            var Q17;
            {var subQ0=sQuery(id+"F2.wireOp",EDGE,"E9.MirrorCS");var subQ4=makeQuery(id+"F3.boolean.opBoolean","COPY",FACE,{"derivedFrom":makeQuery(id+"F3.opExtrude","SWEPT_FACE",FACE,{"disambiguationData":[OSD([subQ0])]})});Q17=makeQuery(id+"FfLhC88wAqj1xS8_1.8.F3.boolean.opBoolean","INTERSECT",EDGE,{"derivedFrom":[makeQuery(id+"FfLhC88wAqj1xS8_1.7.F3.boolean.opBoolean","SPLIT",FACE,{"disambiguationData":[TD([subQ4])],"derivedFrom":makeQuery(id+"FfLhC88wAqj1xS8_1.6.F3.boolean.opBoolean","SPLIT",FACE,{"disambiguationData":[TD([subQ4])],"derivedFrom":makeQuery(id+"FfLhC88wAqj1xS8_1.5.F3.boolean.opBoolean","SPLIT",FACE,{"disambiguationData":[TD([subQ4])],"derivedFrom":makeQuery(id+"FfLhC88wAqj1xS8_1.4.F3.boolean.opBoolean","SPLIT",FACE,{"disambiguationData":[TD([subQ4])],"derivedFrom":makeQuery(id+"FfLhC88wAqj1xS8_1.3.F3.boolean.opBoolean","SPLIT",FACE,{"disambiguationData":[TD([subQ4])],"derivedFrom":makeQuery(id+"FfLhC88wAqj1xS8_1.2.F3.boolean.opBoolean","SPLIT",FACE,{"disambiguationData":[TD([subQ4])],"derivedFrom":makeQuery(id+"FfLhC88wAqj1xS8_1.1.F3.boolean.opBoolean","SPLIT",FACE,{"disambiguationData":[TD([subQ4])],"derivedFrom":makeQuery(id+"F1.opRevolve","SWEPT_FACE",FACE,{"disambiguationData":[OSD([sQuery(id+"F0.wireOp",EDGE,"E1")])]})})})})})})})}),makeQuery(id+"FfLhC88wAqj1xS8_1.8.F3.opExtrude","SWEPT_FACE",FACE,{"disambiguationData":[OSD([subQ0])]})]});}
            var Q18;
            {var subQ0=sQuery(id+"F2.wireOp",EDGE,"E7");var subQ3=makeQuery(id+"F3.boolean.opBoolean","COPY",FACE,{"derivedFrom":makeQuery(id+"F3.opExtrude","SWEPT_FACE",FACE,{"disambiguationData":[OSD([sQuery(id+"F2.wireOp",EDGE,"E9.MirrorCS")])]})});Q18=makeQuery(id+"FfLhC88wAqj1xS8_1.7.F3.boolean.opBoolean","INTERSECT",EDGE,{"derivedFrom":[makeQuery(id+"FfLhC88wAqj1xS8_1.6.F3.boolean.opBoolean","SPLIT",FACE,{"disambiguationData":[TD([subQ3])],"derivedFrom":makeQuery(id+"FfLhC88wAqj1xS8_1.5.F3.boolean.opBoolean","SPLIT",FACE,{"disambiguationData":[TD([subQ3])],"derivedFrom":makeQuery(id+"FfLhC88wAqj1xS8_1.4.F3.boolean.opBoolean","SPLIT",FACE,{"disambiguationData":[TD([subQ3])],"derivedFrom":makeQuery(id+"FfLhC88wAqj1xS8_1.3.F3.boolean.opBoolean","SPLIT",FACE,{"disambiguationData":[TD([subQ3])],"derivedFrom":makeQuery(id+"FfLhC88wAqj1xS8_1.2.F3.boolean.opBoolean","SPLIT",FACE,{"disambiguationData":[TD([subQ3])],"derivedFrom":makeQuery(id+"FfLhC88wAqj1xS8_1.1.F3.boolean.opBoolean","SPLIT",FACE,{"disambiguationData":[TD([subQ3])],"derivedFrom":makeQuery(id+"F1.opRevolve","SWEPT_FACE",FACE,{"disambiguationData":[OSD([sQuery(id+"F0.wireOp",EDGE,"E1")])]})})})})})})}),makeQuery(id+"FfLhC88wAqj1xS8_1.7.F3.opExtrude","SWEPT_FACE",FACE,{"disambiguationData":[OSD([subQ0])]})]});}
            var Q19;
            {var subQ0=sQuery(id+"F2.wireOp",EDGE,"E9.MirrorCS");var subQ3=makeQuery(id+"F3.boolean.opBoolean","COPY",FACE,{"derivedFrom":makeQuery(id+"F3.opExtrude","SWEPT_FACE",FACE,{"disambiguationData":[OSD([subQ0])]})});Q19=makeQuery(id+"FfLhC88wAqj1xS8_1.7.F3.boolean.opBoolean","INTERSECT",EDGE,{"derivedFrom":[makeQuery(id+"FfLhC88wAqj1xS8_1.6.F3.boolean.opBoolean","SPLIT",FACE,{"disambiguationData":[TD([subQ3])],"derivedFrom":makeQuery(id+"FfLhC88wAqj1xS8_1.5.F3.boolean.opBoolean","SPLIT",FACE,{"disambiguationData":[TD([subQ3])],"derivedFrom":makeQuery(id+"FfLhC88wAqj1xS8_1.4.F3.boolean.opBoolean","SPLIT",FACE,{"disambiguationData":[TD([subQ3])],"derivedFrom":makeQuery(id+"FfLhC88wAqj1xS8_1.3.F3.boolean.opBoolean","SPLIT",FACE,{"disambiguationData":[TD([subQ3])],"derivedFrom":makeQuery(id+"FfLhC88wAqj1xS8_1.2.F3.boolean.opBoolean","SPLIT",FACE,{"disambiguationData":[TD([subQ3])],"derivedFrom":makeQuery(id+"FfLhC88wAqj1xS8_1.1.F3.boolean.opBoolean","SPLIT",FACE,{"disambiguationData":[TD([subQ3])],"derivedFrom":makeQuery(id+"F1.opRevolve","SWEPT_FACE",FACE,{"disambiguationData":[OSD([sQuery(id+"F0.wireOp",EDGE,"E1")])]})})})})})})}),makeQuery(id+"FfLhC88wAqj1xS8_1.7.F3.opExtrude","SWEPT_FACE",FACE,{"disambiguationData":[OSD([subQ0])]})]});}
            var Q20;
            {var subQ0=sQuery(id+"F2.wireOp",EDGE,"E7");var subQ3=makeQuery(id+"F3.boolean.opBoolean","COPY",FACE,{"derivedFrom":makeQuery(id+"F3.opExtrude","SWEPT_FACE",FACE,{"disambiguationData":[OSD([sQuery(id+"F2.wireOp",EDGE,"E9.MirrorCS")])]})});Q20=makeQuery(id+"FfLhC88wAqj1xS8_1.6.F3.boolean.opBoolean","INTERSECT",EDGE,{"derivedFrom":[makeQuery(id+"FfLhC88wAqj1xS8_1.5.F3.boolean.opBoolean","SPLIT",FACE,{"disambiguationData":[TD([subQ3])],"derivedFrom":makeQuery(id+"FfLhC88wAqj1xS8_1.4.F3.boolean.opBoolean","SPLIT",FACE,{"disambiguationData":[TD([subQ3])],"derivedFrom":makeQuery(id+"FfLhC88wAqj1xS8_1.3.F3.boolean.opBoolean","SPLIT",FACE,{"disambiguationData":[TD([subQ3])],"derivedFrom":makeQuery(id+"FfLhC88wAqj1xS8_1.2.F3.boolean.opBoolean","SPLIT",FACE,{"disambiguationData":[TD([subQ3])],"derivedFrom":makeQuery(id+"FfLhC88wAqj1xS8_1.1.F3.boolean.opBoolean","SPLIT",FACE,{"disambiguationData":[TD([subQ3])],"derivedFrom":makeQuery(id+"F1.opRevolve","SWEPT_FACE",FACE,{"disambiguationData":[OSD([sQuery(id+"F0.wireOp",EDGE,"E1")])]})})})})})}),makeQuery(id+"FfLhC88wAqj1xS8_1.6.F3.opExtrude","SWEPT_FACE",FACE,{"disambiguationData":[OSD([subQ0])]})]});}
            var Q21;
            {var subQ0=sQuery(id+"F2.wireOp",EDGE,"E9.MirrorCS");var subQ3=makeQuery(id+"F3.boolean.opBoolean","COPY",FACE,{"derivedFrom":makeQuery(id+"F3.opExtrude","SWEPT_FACE",FACE,{"disambiguationData":[OSD([subQ0])]})});Q21=makeQuery(id+"FfLhC88wAqj1xS8_1.6.F3.boolean.opBoolean","INTERSECT",EDGE,{"derivedFrom":[makeQuery(id+"FfLhC88wAqj1xS8_1.5.F3.boolean.opBoolean","SPLIT",FACE,{"disambiguationData":[TD([subQ3])],"derivedFrom":makeQuery(id+"FfLhC88wAqj1xS8_1.4.F3.boolean.opBoolean","SPLIT",FACE,{"disambiguationData":[TD([subQ3])],"derivedFrom":makeQuery(id+"FfLhC88wAqj1xS8_1.3.F3.boolean.opBoolean","SPLIT",FACE,{"disambiguationData":[TD([subQ3])],"derivedFrom":makeQuery(id+"FfLhC88wAqj1xS8_1.2.F3.boolean.opBoolean","SPLIT",FACE,{"disambiguationData":[TD([subQ3])],"derivedFrom":makeQuery(id+"FfLhC88wAqj1xS8_1.1.F3.boolean.opBoolean","SPLIT",FACE,{"disambiguationData":[TD([subQ3])],"derivedFrom":makeQuery(id+"F1.opRevolve","SWEPT_FACE",FACE,{"disambiguationData":[OSD([sQuery(id+"F0.wireOp",EDGE,"E1")])]})})})})})}),makeQuery(id+"FfLhC88wAqj1xS8_1.6.F3.opExtrude","SWEPT_FACE",FACE,{"disambiguationData":[OSD([subQ0])]})]});}
            var Q22;
            {var subQ0=sQuery(id+"F2.wireOp",EDGE,"E7");var subQ3=makeQuery(id+"F3.boolean.opBoolean","COPY",FACE,{"derivedFrom":makeQuery(id+"F3.opExtrude","SWEPT_FACE",FACE,{"disambiguationData":[OSD([sQuery(id+"F2.wireOp",EDGE,"E9.MirrorCS")])]})});Q22=makeQuery(id+"FfLhC88wAqj1xS8_1.5.F3.boolean.opBoolean","INTERSECT",EDGE,{"derivedFrom":[makeQuery(id+"FfLhC88wAqj1xS8_1.4.F3.boolean.opBoolean","SPLIT",FACE,{"disambiguationData":[TD([subQ3])],"derivedFrom":makeQuery(id+"FfLhC88wAqj1xS8_1.3.F3.boolean.opBoolean","SPLIT",FACE,{"disambiguationData":[TD([subQ3])],"derivedFrom":makeQuery(id+"FfLhC88wAqj1xS8_1.2.F3.boolean.opBoolean","SPLIT",FACE,{"disambiguationData":[TD([subQ3])],"derivedFrom":makeQuery(id+"FfLhC88wAqj1xS8_1.1.F3.boolean.opBoolean","SPLIT",FACE,{"disambiguationData":[TD([subQ3])],"derivedFrom":makeQuery(id+"F1.opRevolve","SWEPT_FACE",FACE,{"disambiguationData":[OSD([sQuery(id+"F0.wireOp",EDGE,"E1")])]})})})})}),makeQuery(id+"FfLhC88wAqj1xS8_1.5.F3.opExtrude","SWEPT_FACE",FACE,{"disambiguationData":[OSD([subQ0])]})]});}
            var Q23;
            {var subQ0=sQuery(id+"F2.wireOp",EDGE,"E9.MirrorCS");var subQ3=makeQuery(id+"F3.boolean.opBoolean","COPY",FACE,{"derivedFrom":makeQuery(id+"F3.opExtrude","SWEPT_FACE",FACE,{"disambiguationData":[OSD([subQ0])]})});Q23=makeQuery(id+"FfLhC88wAqj1xS8_1.5.F3.boolean.opBoolean","INTERSECT",EDGE,{"derivedFrom":[makeQuery(id+"FfLhC88wAqj1xS8_1.4.F3.boolean.opBoolean","SPLIT",FACE,{"disambiguationData":[TD([subQ3])],"derivedFrom":makeQuery(id+"FfLhC88wAqj1xS8_1.3.F3.boolean.opBoolean","SPLIT",FACE,{"disambiguationData":[TD([subQ3])],"derivedFrom":makeQuery(id+"FfLhC88wAqj1xS8_1.2.F3.boolean.opBoolean","SPLIT",FACE,{"disambiguationData":[TD([subQ3])],"derivedFrom":makeQuery(id+"FfLhC88wAqj1xS8_1.1.F3.boolean.opBoolean","SPLIT",FACE,{"disambiguationData":[TD([subQ3])],"derivedFrom":makeQuery(id+"F1.opRevolve","SWEPT_FACE",FACE,{"disambiguationData":[OSD([sQuery(id+"F0.wireOp",EDGE,"E1")])]})})})})}),makeQuery(id+"FfLhC88wAqj1xS8_1.5.F3.opExtrude","SWEPT_FACE",FACE,{"disambiguationData":[OSD([subQ0])]})]});}
            var Q24;
            {var subQ0=sQuery(id+"F2.wireOp",EDGE,"E7");var subQ3=makeQuery(id+"F3.boolean.opBoolean","COPY",FACE,{"derivedFrom":makeQuery(id+"F3.opExtrude","SWEPT_FACE",FACE,{"disambiguationData":[OSD([sQuery(id+"F2.wireOp",EDGE,"E9.MirrorCS")])]})});Q24=makeQuery(id+"FfLhC88wAqj1xS8_1.4.F3.boolean.opBoolean","INTERSECT",EDGE,{"derivedFrom":[makeQuery(id+"FfLhC88wAqj1xS8_1.3.F3.boolean.opBoolean","SPLIT",FACE,{"disambiguationData":[TD([subQ3])],"derivedFrom":makeQuery(id+"FfLhC88wAqj1xS8_1.2.F3.boolean.opBoolean","SPLIT",FACE,{"disambiguationData":[TD([subQ3])],"derivedFrom":makeQuery(id+"FfLhC88wAqj1xS8_1.1.F3.boolean.opBoolean","SPLIT",FACE,{"disambiguationData":[TD([subQ3])],"derivedFrom":makeQuery(id+"F1.opRevolve","SWEPT_FACE",FACE,{"disambiguationData":[OSD([sQuery(id+"F0.wireOp",EDGE,"E1")])]})})})}),makeQuery(id+"FfLhC88wAqj1xS8_1.4.F3.opExtrude","SWEPT_FACE",FACE,{"disambiguationData":[OSD([subQ0])]})]});}
            var Q25;
            {var subQ0=sQuery(id+"F2.wireOp",EDGE,"E9.MirrorCS");var subQ4=makeQuery(id+"F3.boolean.opBoolean","COPY",FACE,{"derivedFrom":makeQuery(id+"F3.opExtrude","SWEPT_FACE",FACE,{"disambiguationData":[OSD([subQ0])]})});Q25=makeQuery(id+"FfLhC88wAqj1xS8_1.4.F3.boolean.opBoolean","INTERSECT",EDGE,{"derivedFrom":[makeQuery(id+"FfLhC88wAqj1xS8_1.3.F3.boolean.opBoolean","SPLIT",FACE,{"disambiguationData":[TD([subQ4])],"derivedFrom":makeQuery(id+"FfLhC88wAqj1xS8_1.2.F3.boolean.opBoolean","SPLIT",FACE,{"disambiguationData":[TD([subQ4])],"derivedFrom":makeQuery(id+"FfLhC88wAqj1xS8_1.1.F3.boolean.opBoolean","SPLIT",FACE,{"disambiguationData":[TD([subQ4])],"derivedFrom":makeQuery(id+"F1.opRevolve","SWEPT_FACE",FACE,{"disambiguationData":[OSD([sQuery(id+"F0.wireOp",EDGE,"E1")])]})})})}),makeQuery(id+"FfLhC88wAqj1xS8_1.4.F3.opExtrude","SWEPT_FACE",FACE,{"disambiguationData":[OSD([subQ0])]})]});}
            var Q26;
            {var subQ0=sQuery(id+"F2.wireOp",EDGE,"E7");var subQ3=makeQuery(id+"F3.boolean.opBoolean","COPY",FACE,{"derivedFrom":makeQuery(id+"F3.opExtrude","SWEPT_FACE",FACE,{"disambiguationData":[OSD([sQuery(id+"F2.wireOp",EDGE,"E9.MirrorCS")])]})});Q26=makeQuery(id+"FfLhC88wAqj1xS8_1.3.F3.boolean.opBoolean","INTERSECT",EDGE,{"derivedFrom":[makeQuery(id+"FfLhC88wAqj1xS8_1.2.F3.boolean.opBoolean","SPLIT",FACE,{"disambiguationData":[TD([subQ3])],"derivedFrom":makeQuery(id+"FfLhC88wAqj1xS8_1.1.F3.boolean.opBoolean","SPLIT",FACE,{"disambiguationData":[TD([subQ3])],"derivedFrom":makeQuery(id+"F1.opRevolve","SWEPT_FACE",FACE,{"disambiguationData":[OSD([sQuery(id+"F0.wireOp",EDGE,"E1")])]})})}),makeQuery(id+"FfLhC88wAqj1xS8_1.3.F3.opExtrude","SWEPT_FACE",FACE,{"disambiguationData":[OSD([subQ0])]})]});}
            var Q27;
            {var subQ0=sQuery(id+"F2.wireOp",EDGE,"E7");Q27=makeQuery(id+"FfLhC88wAqj1xS8_1.2.F3.boolean.opBoolean","INTERSECT",EDGE,{"derivedFrom":[makeQuery(id+"FfLhC88wAqj1xS8_1.1.F3.boolean.opBoolean","SPLIT",FACE,{"disambiguationData":[TD([makeQuery(id+"F3.boolean.opBoolean","COPY",FACE,{"derivedFrom":makeQuery(id+"F3.opExtrude","SWEPT_FACE",FACE,{"disambiguationData":[OSD([sQuery(id+"F2.wireOp",EDGE,"E9.MirrorCS")])]})})])],"derivedFrom":makeQuery(id+"F1.opRevolve","SWEPT_FACE",FACE,{"disambiguationData":[OSD([sQuery(id+"F0.wireOp",EDGE,"E1")])]})}),makeQuery(id+"FfLhC88wAqj1xS8_1.2.F3.opExtrude","SWEPT_FACE",FACE,{"disambiguationData":[OSD([subQ0])]})]});}
            var Q28;
            {var subQ0=sQuery(id+"F2.wireOp",EDGE,"E9.MirrorCS");var subQ4=makeQuery(id+"F3.boolean.opBoolean","COPY",FACE,{"derivedFrom":makeQuery(id+"F3.opExtrude","SWEPT_FACE",FACE,{"disambiguationData":[OSD([subQ0])]})});Q28=makeQuery(id+"FfLhC88wAqj1xS8_1.3.F3.boolean.opBoolean","INTERSECT",EDGE,{"derivedFrom":[makeQuery(id+"FfLhC88wAqj1xS8_1.2.F3.boolean.opBoolean","SPLIT",FACE,{"disambiguationData":[TD([subQ4])],"derivedFrom":makeQuery(id+"FfLhC88wAqj1xS8_1.1.F3.boolean.opBoolean","SPLIT",FACE,{"disambiguationData":[TD([subQ4])],"derivedFrom":makeQuery(id+"F1.opRevolve","SWEPT_FACE",FACE,{"disambiguationData":[OSD([sQuery(id+"F0.wireOp",EDGE,"E1")])]})})}),makeQuery(id+"FfLhC88wAqj1xS8_1.3.F3.opExtrude","SWEPT_FACE",FACE,{"disambiguationData":[OSD([subQ0])]})]});}
            var Q29;
            {var subQ0=sQuery(id+"F2.wireOp",EDGE,"E9.MirrorCS");Q29=makeQuery(id+"FfLhC88wAqj1xS8_1.2.F3.boolean.opBoolean","INTERSECT",EDGE,{"derivedFrom":[makeQuery(id+"FfLhC88wAqj1xS8_1.1.F3.boolean.opBoolean","SPLIT",FACE,{"disambiguationData":[TD([makeQuery(id+"F3.boolean.opBoolean","COPY",FACE,{"derivedFrom":makeQuery(id+"F3.opExtrude","SWEPT_FACE",FACE,{"disambiguationData":[OSD([subQ0])]})})])],"derivedFrom":makeQuery(id+"F1.opRevolve","SWEPT_FACE",FACE,{"disambiguationData":[OSD([sQuery(id+"F0.wireOp",EDGE,"E1")])]})}),makeQuery(id+"FfLhC88wAqj1xS8_1.2.F3.opExtrude","SWEPT_FACE",FACE,{"disambiguationData":[OSD([subQ0])]})]});}
            var Q30;
            Q30=makeQuery(id+"FfLhC88wAqj1xS8_1.1.F3.boolean.opBoolean","INTERSECT",EDGE,{"derivedFrom":[makeQuery(id+"F1.opRevolve","SWEPT_FACE",FACE,{"disambiguationData":[OSD([sQuery(id+"F0.wireOp",EDGE,"E1")])]}),makeQuery(id+"FfLhC88wAqj1xS8_1.1.F3.opExtrude","SWEPT_FACE",FACE,{"disambiguationData":[OSD([sQuery(id+"F2.wireOp",EDGE,"E7")])]})]});
            var Q31;
            Q31=makeQuery(id+"FfLhC88wAqj1xS8_1.1.F3.boolean.opBoolean","INTERSECT",EDGE,{"derivedFrom":[makeQuery(id+"F1.opRevolve","SWEPT_FACE",FACE,{"disambiguationData":[OSD([sQuery(id+"F0.wireOp",EDGE,"E1")])]}),makeQuery(id+"FfLhC88wAqj1xS8_1.1.F3.opExtrude","SWEPT_FACE",FACE,{"disambiguationData":[OSD([sQuery(id+"F2.wireOp",EDGE,"E9.MirrorCS")])]})]});
            fillet(context, id + "F4", {"entities" : qUnion([Q0, Q1, Q2, Q3, Q4, Q5, Q6, Q7, Q8, Q9, Q10, Q11, Q12, Q13, Q14, Q15, Q16, Q17, Q18, Q19, Q20, Q21, Q22, Q23, Q24, Q25, Q26, Q27, Q28, Q29, Q30, Q31]), "radius" : 4.57 * mm, "tangentPropagation" : true, "allowEdgeOverflow" : false});
        }
        {
            var Q0;
            Q0=qCreatedBy(makeId("Front.planeOp"),FACE);
            var sketch = newSketch(context, id + "F5", { "sketchPlane" : qUnion([Q0])});
            skCircle(sketch, "E14", {"center": v(0, 38.1) * mm, "radius": 3.18 * mm});
            skSolve(sketch);
        }
        {
            var Q0;
            Q0=makeQuery(id+"F5.imprint","IMPRINT",FACE,{"disambiguationData":[TD([[makeQuery(id+"F5.imprint","IMPRINT",EDGE,{"derivedFrom":sQuery(id+"F5.wireOp",EDGE,"E14")}),1.0]])]});
            extrude(context, id + "F6", {"entities" : qUnion([Q0]), "operationType" : NewBodyOperationType.REMOVE, "oppositeDirection" : true, "depth" : 6.35 * mm, "offsetDistance" : 25.4 * mm});
        }
    });
